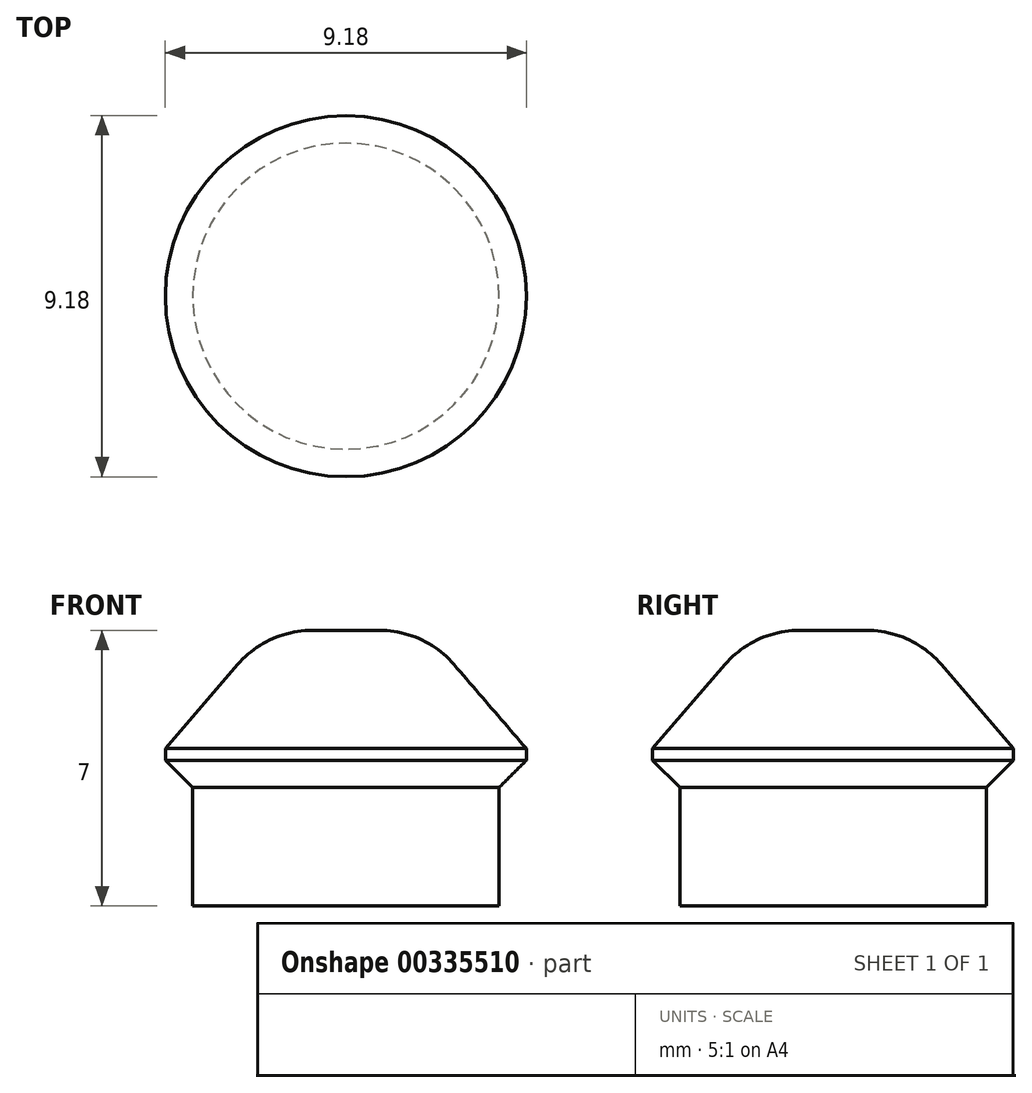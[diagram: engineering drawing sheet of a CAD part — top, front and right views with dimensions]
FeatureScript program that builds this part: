
annotation { "Feature Type Name" : "Feature", "Feature Type Description" : "" }
export const myFeature = defineFeature(function(context is Context, id is Id, definition is map)
    precondition{}
    {
        {
            var Q0;
            Q0=qCreatedBy(makeId("Top.planeOp"),FACE);
            var sketch = newSketch(context, id + "F0", { "sketchPlane" : qUnion([Q0])});
            skCircle(sketch, "E0", {"center": v(0, 0) * mm, "radius": 3.9 * mm});
            skSolve(sketch);
        }
        {
            var Q0;
            Q0=makeQuery(id+"F0.imprint","IMPRINT",FACE,{"disambiguationData":[TD([[makeQuery(id+"F0.imprint","IMPRINT",EDGE,{"derivedFrom":sQuery(id+"F0.wireOp",EDGE,"E0")}),1.0]])]});
            extrude(context, id + "F1", {"entities" : qUnion([Q0]), "depth" : 3 * mm});
        }
        {
            var Q0;
            Q0=makeQuery(id+"F1.opExtrude","CAP_FACE",FACE,{"disambiguationData":[OSD([sQuery(id+"F0.wireOp",EDGE,"E0")])],"isStart":false});
            var sketch = newSketch(context, id + "F2", { "sketchPlane" : qUnion([Q0])});
            skCircle(sketch, "E1", {"center": v(0, 0) * mm, "radius": 4.58 * mm});
            skSolve(sketch);
        }
        {
            var Q0;
            Q0=makeQuery(id+"F2.imprint","IMPRINT",FACE,{"disambiguationData":[TD([[makeQuery(id+"F2.imprint","IMPRINT",EDGE,{"derivedFrom":makeQuery(id+"F1.opExtrude","CAP_EDGE",EDGE,{"disambiguationData":[OSD([sQuery(id+"F0.wireOp",EDGE,"E0")])],"isStart":false})}),1.0]])]});
            cPlane(context, id + "F3", {"entities" : qUnion([Q0]), "cplaneType" : CPlaneType.OFFSET, "offset" : 4 * mm, "width" : 150 * mm, "height" : 150 * mm});
        }
        {
            var Q0;
            Q0=qCreatedBy(id+"F3.planeOp",FACE);
            var sketch = newSketch(context, id + "F4", { "sketchPlane" : qUnion([Q0])});
            skCircle(sketch, "E2", {"center": v(0, 0) * mm, "radius": 2 * mm});
            skSolve(sketch);
        }
        {
            var Q0;
            Q0=makeQuery(id+"F2.imprint","IMPRINT",FACE,{"disambiguationData":[TD([[makeQuery(id+"F2.imprint","IMPRINT",EDGE,{"derivedFrom":makeQuery(id+"F1.opExtrude","CAP_EDGE",EDGE,{"disambiguationData":[OSD([sQuery(id+"F0.wireOp",EDGE,"E0")])],"isStart":false})}),1.0]])]});
            var Q1;
            Q1=makeQuery(id+"F2.imprint","IMPRINT",FACE,{"disambiguationData":[TD([[makeQuery(id+"F2.imprint","IMPRINT",EDGE,{"derivedFrom":sQuery(id+"F2.wireOp",EDGE,"E1")}),1.0]])]});
            extrude(context, id + "F5", {"entities" : qUnion([Q0, Q1]), "operationType" : NewBodyOperationType.ADD, "depth" : 1 * mm});
        }
        {
            var Q1;
            Q1=makeQuery(id+"F5.opExtrude","CAP_FACE",FACE,{"disambiguationData":[OSD([sQuery(id+"F2.wireOp",EDGE,"E1")])],"isStart":false});
            var Q2;
            Q2=makeQuery(id+"F4.imprint","IMPRINT",FACE,{"disambiguationData":[TD([[makeQuery(id+"F4.imprint","IMPRINT",EDGE,{"derivedFrom":sQuery(id+"F4.wireOp",EDGE,"E2")}),1.0]])]});
            loft(context, id + "F6", {"operationType" : NewBodyOperationType.ADD, "sheetProfilesArray" : [{ "sheetProfileEntities" : qUnion([Q1]) }, { "sheetProfileEntities" : qUnion([Q2]) }]});
        }
        {
            var Q0;
            Q0=makeQuery(id+"F6.opLoft","MID_CAP_EDGE",EDGE,{"disambiguationData":[OSD([sQuery(id+"F2.wireOp",EDGE,"E1"),sQuery(id+"F4.wireOp",EDGE,"E2")])],"capPos":1.0});
            fillet(context, id + "F7", {"entities" : qUnion([Q0]), "radius" : 2.5 * mm, "tangentPropagation" : true, "allowEdgeOverflow" : false});
        }
        {
            var Q0;
            Q0=makeQuery(id+"F5.opExtrude","CAP_EDGE",EDGE,{"disambiguationData":[OSD([sQuery(id+"F2.wireOp",EDGE,"E1")])],"isStart":true});
            chamfer(context, id + "F8", {"entities" : qUnion([Q0]), "width" : .7 * mm, "tangentPropagation" : true});
        }
    });
